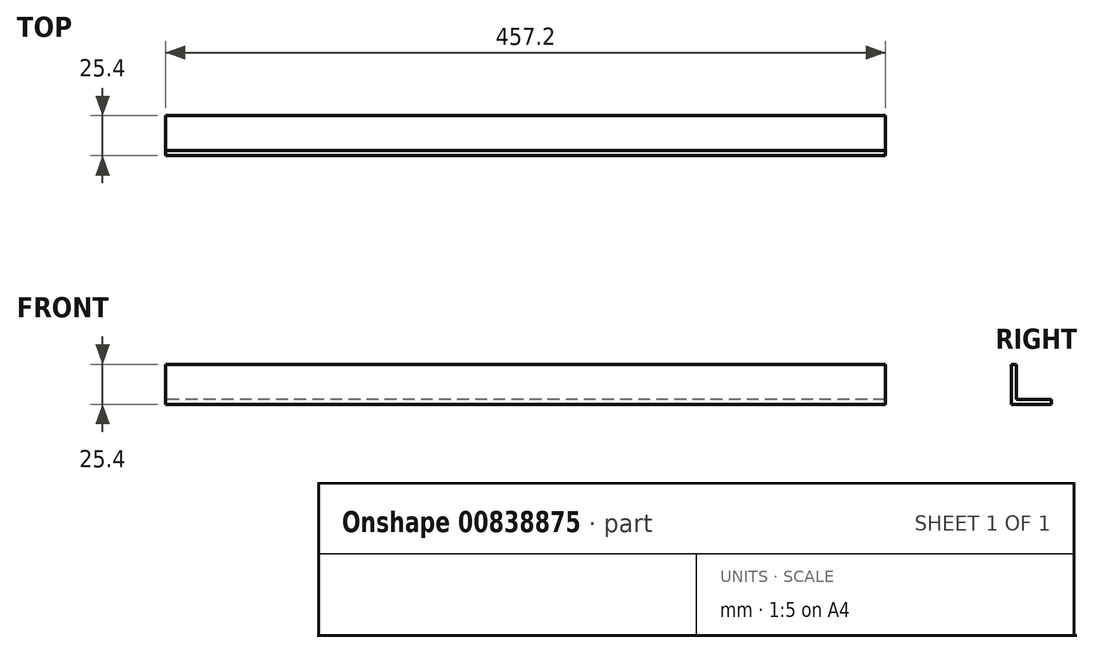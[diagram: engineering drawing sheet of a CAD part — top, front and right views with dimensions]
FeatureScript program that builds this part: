
annotation { "Feature Type Name" : "Feature", "Feature Type Description" : "" }
export const myFeature = defineFeature(function(context is Context, id is Id, definition is map)
    precondition{}
    {
        {
            var Q0;
            Q0=qCreatedBy(makeId("Right.planeOp"),FACE);
            var sketch = newSketch(context, id + "F0", { "sketchPlane" : qUnion([Q0])});
            skLineSegment(sketch, "E0", {"start": v(0, 0) * mm, "end": v(0, 25.4) * mm});
            skLineSegment(sketch, "E1", {"start": v(0, 25.4) * mm, "end": v(3.17, 25.4) * mm});
            skLineSegment(sketch, "E2", {"start": v(3.17, 25.4) * mm, "end": v(3.18, 3.17) * mm});
            skLineSegment(sketch, "E3", {"start": v(3.18, 3.17) * mm, "end": v(25.4, 3.18) * mm});
            skLineSegment(sketch, "E4", {"start": v(25.4, 3.18) * mm, "end": v(25.4, 0) * mm});
            skLineSegment(sketch, "E5", {"start": v(25.4, 0) * mm, "end": v(0, 0) * mm});
            skSolve(sketch);
        }
        {
            var Q0;
            Q0=makeQuery(id+"F0.imprint","IMPRINT",FACE,{"disambiguationData":[TD([[makeQuery(id+"F0.imprint","IMPRINT",EDGE,{"derivedFrom":sQuery(id+"F0.wireOp",EDGE,"E0")}),-1.0]])]});
            extrude(context, id + "F1", {"entities" : qUnion([Q0]), "depth" : 457.2 * mm, "offsetDistance" : 25.4 * mm});
        }
    });
